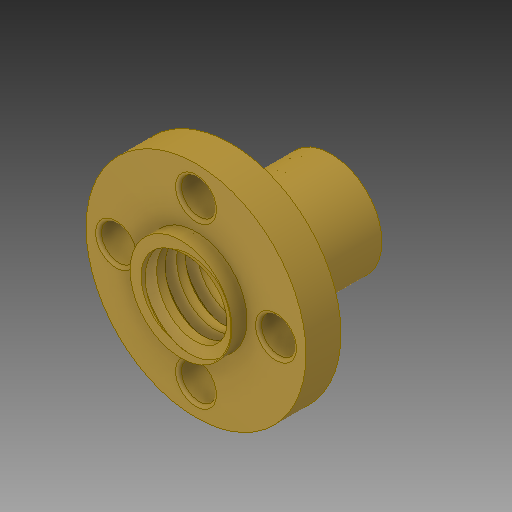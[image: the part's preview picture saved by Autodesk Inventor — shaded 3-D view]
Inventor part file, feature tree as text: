
AUTODESK INVENTOR PART (.ipt)
format: ipt  version: 2019 (Build 230136000, 136)  size: 388,608 bytes
history: native  units: in
note: dims shown in document units (in); Inventor stores cm internally (conversion verified against a paired STEP export)
features: other x1, fillet x1
ambient origin geometry x8: Origin, YZ Plane, XZ Plane, XY Plane, X Axis, Y Axis, Z Axis, Center Point
bodies: Solid1 (feature_tree)
feature tree (2):
  other  "LeadScrew Nut 8mm x 2mmPitch.STEP"
  fillet  "Fillet2"  [1 undecoded]
note: 1 required parameter value undecoded (feature->parameter linkage not recoverable at this tier; creation-order binding heuristic only, values carry confidence <= 0.55)
